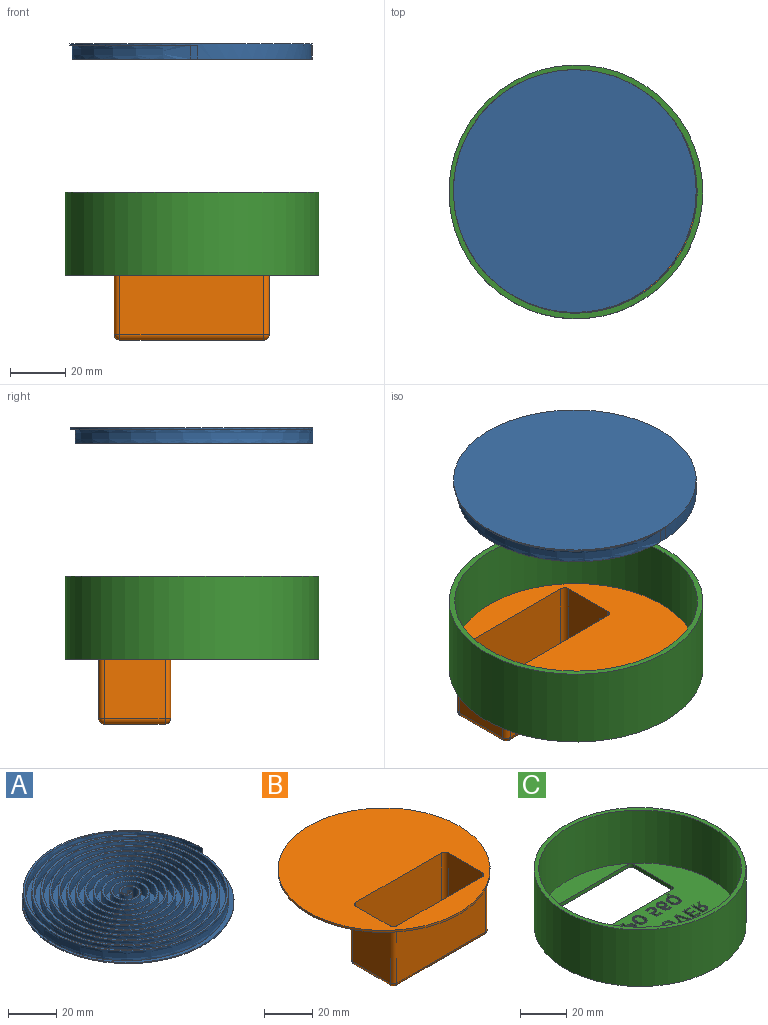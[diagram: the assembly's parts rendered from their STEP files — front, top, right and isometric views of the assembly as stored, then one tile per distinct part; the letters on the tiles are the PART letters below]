
ASSEMBLY  parts=3 mates=2
PART A: 9 faces, bbox 87.8x87.8x5.5 mm
  f0: plane 87.8x87.8mm, normal (0,0,1), area 4541mm2, adj f2,f3,f4,f5,f6,f7
  f1: plane 87.8x87.8mm, normal (0,0,-1), area 6054.5mm2, adj f2
  f2: cylinder r=43.9mm len=87.8mm, axis (0,0,1), area 450.2mm2, adj f0,f1,f3,f4,f8
  f3: cylinder r=43.87mm len=5mm, axis (0,0,-1), area 19.8mm2, adj f0,f2,f7,f8
  f4: cylinder r=43.3mm len=5mm, axis (0,0,-1), area 12.8mm2, adj f0,f2,f5,f8
  f5: extruded ~82.3x76.86mm, area 8343.7mm2, adj f0,f4,f6,f8
  f6: plane 5x0.36mm, normal (-0.71,-0.71,0), area 2.6mm2, adj f0,f5,f7,f8
  f7: extruded ~82.3x76.86mm, area 8343.7mm2, adj f0,f3,f6,f8
  f8: plane 86.84x85.93mm, normal (0,0,1), area 1513.4mm2, adj f2,f3,f4,f5,f6,f7
PART B: 38 faces, bbox 87.8x87.8x30 mm
  f0: plane 87.8x87.8mm, normal (0,0,1), area 4761.9mm2, adj f1,f12,f13,f14,f15,f16,f17,f18
  f1: cylinder r=43.9mm len=87.8mm, axis (0,0,1), area 275.8mm2, adj f0,f2
  f2: plane 87.8x87.8mm, normal (0,0,-1), area 4601.9mm2, adj f1,f3,f4,f5,f6,f7,f8,f9
  f3: plane 52x27mm, normal (0,1,0), area 1404mm2, adj f2,f4,f10,f33
  f4: cylinder r=2mm len=27mm, axis (0,0,1), area 84.8mm2, adj f2,f3,f5,f31
  f5: plane 27x22mm, normal (-1,0,0), area 586.9mm2, adj f2,f4,f6,f29,f37
  f6: cylinder r=2mm len=27mm, axis (0,0,1), area 84.8mm2, adj f2,f5,f7,f30
  f7: plane 52x27mm, normal (0,-1,0), area 1404mm2, adj f2,f6,f8,f32
  f8: cylinder r=2mm len=27mm, axis (0,0,1), area 84.8mm2, adj f2,f7,f9,f34
  f9: plane 27x22mm, normal (1,0,0), area 594mm2, adj f2,f8,f10,f36
  f10: cylinder r=2mm len=27mm, axis (0,0,1), area 84.8mm2, adj f2,f3,f9,f35
  f11: plane 52x22mm, normal (0,0,-1), area 1144mm2, adj f29,f32,f33,f36
  f12: plane 50x27mm, normal (0,-1,0), area 1350mm2, adj f0,f13,f19,f25
  f13: cylinder r=2mm len=27mm, axis (0,0,1), area 84.8mm2, adj f0,f12,f14,f23
  f14: plane 27x20mm, normal (1,0,0), area 532.9mm2, adj f0,f13,f15,f21,f37
  f15: cylinder r=2mm len=27mm, axis (0,0,1), area 84.8mm2, adj f0,f14,f16,f22
  f16: plane 50x27mm, normal (0,1,0), area 1350mm2, adj f0,f15,f17,f24
  f17: cylinder r=2mm len=27mm, axis (0,0,1), area 84.8mm2, adj f0,f16,f18,f26
  f18: plane 27x20mm, normal (-1,0,0), area 540mm2, adj f0,f17,f19,f28
  f19: cylinder r=2mm len=27mm, axis (0,0,1), area 84.8mm2, adj f0,f12,f18,f27
  f20: plane 50x20mm, normal (0,0,1), area 1000mm2, adj f21,f24,f25,f28
  f21: cylinder r=2mm len=20mm, axis (0,-1,0), area 62.8mm2, adj f14,f20,f22,f23
  f22: sphere r=2mm, area 6.3mm2, adj f15,f21,f24
  f23: sphere r=2mm, area 6.3mm2, adj f13,f21,f25
  f24: cylinder r=2mm len=50mm, axis (1,0,0), area 157.1mm2, adj f16,f20,f22,f26
  f25: cylinder r=2mm len=50mm, axis (-1,0,0), area 157.1mm2, adj f12,f20,f23,f27
  f26: sphere r=2mm, area 6.3mm2, adj f17,f24,f28
  f27: sphere r=2mm, area 6.3mm2, adj f19,f25,f28
  f28: cylinder r=2mm len=20mm, axis (0,1,0), area 62.8mm2, adj f18,f20,f26,f27
  f29: cylinder r=2mm len=22mm, axis (0,1,0), area 69.1mm2, adj f5,f11,f30,f31
  f30: sphere r=2mm, area 6.3mm2, adj f6,f29,f32
  f31: sphere r=2mm, area 6.3mm2, adj f4,f29,f33
  f32: cylinder r=2mm len=52mm, axis (-1,0,0), area 163.4mm2, adj f7,f11,f30,f34
  f33: cylinder r=2mm len=52mm, axis (1,0,0), area 163.4mm2, adj f3,f11,f31,f35
  f34: sphere r=2mm, area 6.3mm2, adj f8,f32,f36
  f35: sphere r=2mm, area 6.3mm2, adj f10,f33,f36
  f36: cylinder r=2mm len=22mm, axis (0,-1,0), area 69.1mm2, adj f9,f11,f34,f35
  f37: cylinder r=1.5mm len=3mm, axis (-1,0,0), area 9.4mm2, adj f5,f14
PART C: 428 faces, bbox 91.8x91.8x30 mm
  f0: plane 91.8x91.8mm, normal (0,0,-1), area 4849.9mm2, adj f4,f5,f6,f7,f8,f9,f10,f11
  f1: plane 87.8x87.8mm, normal (0,0,1), area 4285.7mm2, adj f2,f5,f6,f7,f8,f9,f10,f11
  f2: cylinder r=43.9mm len=87.8mm, axis (0,0,1), area 7723.3mm2, adj f1,f3
  f3: plane 91.8x91.8mm, normal (0,0,1), area 564.2mm2, adj f2,f4
  f4: cylinder r=45.9mm len=91.8mm, axis (0,0,1), area 8651.9mm2, adj f0,f3
  f5: cylinder r=2mm len=2mm, axis (0,0,-1), area 6.3mm2, adj f0,f1,f6,f12
  f6: plane 53x2mm, normal (0,1,0), area 106mm2, adj f0,f1,f5,f7
  f7: cylinder r=2mm len=2mm, axis (0,0,-1), area 6.3mm2, adj f0,f1,f6,f8
  f8: plane 23x2mm, normal (1,0,0), area 46mm2, adj f0,f1,f7,f9
  f9: cylinder r=2mm len=2mm, axis (0,0,-1), area 6.3mm2, adj f0,f1,f8,f10
  f10: plane 53x2mm, normal (0,-1,0), area 106mm2, adj f0,f1,f9,f11
  f11: cylinder r=2mm len=2mm, axis (0,0,-1), area 6.3mm2, adj f0,f1,f10,f12
  f12: plane 23x2mm, normal (-1,0,0), area 46mm2, adj f0,f1,f5,f11
  f13: plane 6.76x2mm, normal (1,0,0), area 13.5mm2, adj f0,f1,f14,f16
  f14: plane 2x1.12mm, normal (0,-1,0), area 2.2mm2, adj f0,f1,f13,f15
  f15: plane 6.76x2mm, normal (-1,0,0), area 13.5mm2, adj f0,f1,f14,f16
  f16: plane 2x1.12mm, normal (0,1,0), area 2.2mm2, adj f0,f1,f13,f15
  f17: extruded ~2x1.44mm, area 2.9mm2, adj f0,f1,f18,f37
  f18: extruded ~2x1.06mm, area 2.4mm2, adj f0,f1,f17,f19
  f19: extruded ~2x0.83mm, area 2.2mm2, adj f0,f1,f18,f20
  f20: extruded ~2x1.04mm, area 2.2mm2, adj f0,f1,f19,f21
  f21: plane 2x0.91mm, normal (1,0,0), area 1.8mm2, adj f0,f1,f20,f22
  f22: extruded ~2x0.57mm, area 1.2mm2, adj f0,f1,f21,f23
  f23: extruded ~2x0.48mm, area 1.3mm2, adj f0,f1,f22,f24
  f24: extruded ~2x0.77mm, area 1.7mm2, adj f0,f1,f23,f25
  f25: extruded ~2x1.11mm, area 2.2mm2, adj f0,f1,f24,f26
  f26: extruded ~2x1.11mm, area 2.2mm2, adj f0,f1,f25,f27
  f27: extruded ~2x0.77mm, area 1.7mm2, adj f0,f1,f26,f28
  f28: extruded ~2x0.47mm, area 1.3mm2, adj f0,f1,f27,f29
  f29: extruded ~2x0.58mm, area 1.2mm2, adj f0,f1,f28,f30
  f30: plane 2x1.36mm, normal (1,0,0), area 2.7mm2, adj f0,f1,f29,f31
  f31: plane 2x1.05mm, normal (0.86,-0.5,0), area 2.4mm2, adj f0,f1,f30,f32
  f32: plane 2x1.21mm, normal (0,-1,0), area 2.4mm2, adj f0,f1,f31,f33
  f33: plane 2x1.63mm, normal (-0.79,0.61,0), area 4.1mm2, adj f0,f1,f32,f34
  f34: extruded ~2x0.8mm, area 1.8mm2, adj f0,f1,f33,f35
  f35: extruded ~2x0.71mm, area 1.9mm2, adj f0,f1,f34,f36
  f36: extruded ~2x1mm, area 2.2mm2, adj f0,f1,f35,f37
  f37: extruded ~2x1.27mm, area 2.6mm2, adj f0,f1,f17,f36
  f38: extruded ~2x1.4mm, area 2.8mm2, adj f0,f1,f39,f56
  f39: extruded ~2x1.05mm, area 2.3mm2, adj f0,f1,f38,f40
  f40: extruded ~2x0.78mm, area 2.1mm2, adj f0,f1,f39,f41
  f41: extruded ~2x0.99mm, area 2.1mm2, adj f0,f1,f40,f42
  f42: plane 2x0.17mm, normal (0,-1,0), area 0.3mm2, adj f0,f1,f41,f43
  f43: plane 2x0.89mm, normal (-1,0,0), area 1.8mm2, adj f0,f1,f42,f44
  f44: extruded ~2x0.57mm, area 1.2mm2, adj f0,f1,f43,f45
  f45: extruded ~2x0.48mm, area 1.4mm2, adj f0,f1,f44,f46
  f46: extruded ~2x0.77mm, area 1.7mm2, adj f0,f1,f45,f47
  f47: extruded ~2x1.11mm, area 2.2mm2, adj f0,f1,f46,f48
  f48: extruded ~2x1.11mm, area 2.2mm2, adj f0,f1,f47,f49
  f49: extruded ~2x0.77mm, area 1.7mm2, adj f0,f1,f48,f50
  f50: extruded ~2x0.47mm, area 1.3mm2, adj f0,f1,f49,f51
  f51: extruded ~2x0.58mm, area 1.2mm2, adj f0,f1,f50,f52
  f52: plane 2x0.92mm, normal (-1,0,0), area 1.8mm2, adj f0,f1,f51,f53
  f53: extruded ~2x1.05mm, area 2.2mm2, adj f0,f1,f52,f54
  f54: extruded ~2x0.84mm, area 2.2mm2, adj f0,f1,f53,f55
  f55: extruded ~2x1.06mm, area 2.4mm2, adj f0,f1,f54,f56
  f56: extruded ~2x1.44mm, area 2.9mm2, adj f0,f1,f38,f55
  f57: extruded ~2x0.72mm, area 1.5mm2, adj f0,f1,f58,f87
  f58: extruded ~2x0.57mm, area 1.2mm2, adj f0,f1,f57,f59
  f59: plane 2x0.76mm, normal (-0.91,-0.42,0), area 1.7mm2, adj f0,f1,f58,f60
  f60: extruded ~2x0.78mm, area 1.7mm2, adj f0,f1,f59,f61
  f61: extruded ~2x0.97mm, area 1.9mm2, adj f0,f1,f60,f62
  f62: extruded ~2x0.87mm, area 1.8mm2, adj f0,f1,f61,f63
  f63: extruded ~2x0.79mm, area 2.1mm2, adj f0,f1,f62,f64
  f64: extruded ~2x1.27mm, area 2.8mm2, adj f0,f1,f63,f65
  f65: extruded ~2.01x2mm, area 4.1mm2, adj f0,f1,f64,f66
  f66: extruded ~2x1.06mm, area 2.1mm2, adj f0,f1,f65,f67
  f67: extruded ~2x0.85mm, area 1.9mm2, adj f0,f1,f66,f68
  f68: extruded ~2x0.7mm, area 1.8mm2, adj f0,f1,f67,f69
  f69: extruded ~2x0.98mm, area 2mm2, adj f0,f1,f68,f70
  f70: plane 2x0.9mm, normal (-1,0,0), area 1.8mm2, adj f0,f1,f69,f71
  f71: extruded ~2x0.46mm, area 1mm2, adj f0,f1,f70,f72
  f72: extruded ~2x0.37mm, area 1mm2, adj f0,f1,f71,f73
  f73: extruded ~2x0.45mm, area 1mm2, adj f0,f1,f72,f74
  f74: extruded ~2x0.56mm, area 1.1mm2, adj f0,f1,f73,f75
  f75: extruded ~2x0.55mm, area 1.1mm2, adj f0,f1,f74,f76
  f76: extruded ~2x0.44mm, area 1mm2, adj f0,f1,f75,f77
  f77: extruded ~2x0.37mm, area 1mm2, adj f0,f1,f76,f78
  f78: extruded ~2x0.47mm, area 1mm2, adj f0,f1,f77,f79
  f79: plane 2x0.81mm, normal (-1,0,0), area 1.6mm2, adj f0,f1,f78,f80
  f80: extruded ~2x0.67mm, area 1.4mm2, adj f0,f1,f79,f81
  f81: extruded ~2x0.39mm, area 1.1mm2, adj f0,f1,f80,f82
  f82: extruded ~2x0.04mm, area 0.1mm2, adj f0,f1,f81,f83
  f83: extruded ~2x0.04mm, area 0.1mm2, adj f0,f1,f82,f84
  f84: extruded ~2x0.74mm, area 1.5mm2, adj f0,f1,f83,f85
  f85: extruded ~2x0.63mm, area 1.4mm2, adj f0,f1,f84,f86
  f86: extruded ~2x0.45mm, area 1.3mm2, adj f0,f1,f85,f87
  f87: extruded ~2x0.65mm, area 1.4mm2, adj f0,f1,f57,f86
  f88: plane 2x0.83mm, normal (1,0,0), area 1.7mm2, adj f0,f1,f89,f101
  f89: extruded ~2x0.76mm, area 1.8mm2, adj f0,f1,f88,f90
  f90: extruded ~2x0.95mm, area 2mm2, adj f0,f1,f89,f91
  f91: extruded ~2x0.98mm, area 2.1mm2, adj f0,f1,f90,f92
  f92: extruded ~2x0.76mm, area 1.8mm2, adj f0,f1,f91,f93
  f93: plane 2x0.9mm, normal (1,0,0), area 1.8mm2, adj f0,f1,f92,f94
  f94: extruded ~2x0.68mm, area 1.4mm2, adj f0,f1,f93,f95
  f95: extruded ~2x0.66mm, area 1.6mm2, adj f0,f1,f94,f96
  f96: extruded ~2x0.74mm, area 1.8mm2, adj f0,f1,f95,f97
  f97: extruded ~2x1.11mm, area 2.3mm2, adj f0,f1,f96,f98
  f98: extruded ~2x0.76mm, area 1.5mm2, adj f0,f1,f97,f99
  f99: extruded ~2x0.69mm, area 1.6mm2, adj f0,f1,f98,f100
  f100: extruded ~2x0.64mm, area 1.6mm2, adj f0,f1,f99,f101
  f101: extruded ~2x0.83mm, area 1.7mm2, adj f0,f1,f88,f100
  f102: plane 2x0.83mm, normal (1,0,0), area 1.7mm2, adj f0,f1,f103,f105
  f103: plane 2.73x2mm, normal (0,-1,0), area 5.5mm2, adj f0,f1,f102,f104
  f104: plane 2x0.83mm, normal (-1,0,0), area 1.7mm2, adj f0,f1,f103,f105
  f105: plane 2.73x2mm, normal (0,1,0), area 5.5mm2, adj f0,f1,f102,f104
  f106: plane 2x0.75mm, normal (-1,0,0), area 1.5mm2, adj f0,f1,f107,f109
  f107: plane 2.45x2mm, normal (0,1,0), area 4.9mm2, adj f0,f1,f106,f108
  f108: plane 2x0.75mm, normal (1,0,0), area 1.5mm2, adj f0,f1,f107,f109
  f109: plane 2.45x2mm, normal (0,-1,0), area 4.9mm2, adj f0,f1,f106,f108
  f110: plane 6.76x2mm, normal (1,0,0), area 13.5mm2, adj f0,f1,f111,f113
  f111: plane 2x1.12mm, normal (0,-1,0), area 2.2mm2, adj f0,f1,f110,f112
  f112: plane 6.76x2mm, normal (-1,0,0), area 13.5mm2, adj f0,f1,f111,f113
  f113: plane 2x1.12mm, normal (0,1,0), area 2.2mm2, adj f0,f1,f110,f112
  f114: plane 5x2mm, normal (0.96,0.27,0), area 10.4mm2, adj f0,f1,f115,f118
  f115: plane 2x1.79mm, normal (1,0,0), area 3.6mm2, adj f0,f1,f114,f116
  f116: plane 2x0.48mm, normal (0,-1,0), area 1mm2, adj f0,f1,f115,f117
  f117: plane 6.79x2.2mm, normal (-0.95,-0.31,0), area 14.3mm2, adj f0,f1,f116,f118
  f118: plane 2x1.25mm, normal (0,1,0), area 2.5mm2, adj f0,f1,f114,f117
  f119: plane 6.79x2.1mm, normal (0.96,-0.3,0), area 14.2mm2, adj f0,f1,f120,f123
  f120: plane 2x0.58mm, normal (0,-1,0), area 1.2mm2, adj f0,f1,f119,f121
  f121: plane 2x1.49mm, normal (-1,0,0), area 3mm2, adj f0,f1,f120,f122
  f122: plane 5.3x2mm, normal (-0.97,0.26,0), area 11mm2, adj f0,f1,f121,f123
  f123: plane 2x1.26mm, normal (0,1,0), area 2.5mm2, adj f0,f1,f119,f122
  f124: plane 2x0.91mm, normal (1,0,0), area 1.8mm2, adj f0,f1,f125,f141
  f125: extruded ~2x0.58mm, area 1.2mm2, adj f0,f1,f124,f126
  f126: extruded ~2x0.48mm, area 1.4mm2, adj f0,f1,f125,f127
  f127: extruded ~2x0.77mm, area 1.7mm2, adj f0,f1,f126,f128
  f128: extruded ~2x1.11mm, area 2.2mm2, adj f0,f1,f127,f129
  f129: extruded ~2x1.11mm, area 2.2mm2, adj f0,f1,f128,f130
  f130: extruded ~2x0.77mm, area 1.7mm2, adj f0,f1,f129,f131
  f131: extruded ~2x0.48mm, area 1.3mm2, adj f0,f1,f130,f132
  f132: extruded ~2x0.59mm, area 1.2mm2, adj f0,f1,f131,f133
  f133: plane 2x0.91mm, normal (1,0,0), area 1.8mm2, adj f0,f1,f132,f134
  f134: extruded ~2x1.05mm, area 2.2mm2, adj f0,f1,f133,f135
  f135: extruded ~2x0.83mm, area 2.1mm2, adj f0,f1,f134,f136
  f136: extruded ~2x1.07mm, area 2.4mm2, adj f0,f1,f135,f137
  f137: extruded ~2x1.45mm, area 2.9mm2, adj f0,f1,f136,f138
  f138: extruded ~2x1.44mm, area 2.9mm2, adj f0,f1,f137,f139
  f139: extruded ~2x1.06mm, area 2.4mm2, adj f0,f1,f138,f140
  f140: extruded ~2x0.83mm, area 2.2mm2, adj f0,f1,f139,f141
  f141: extruded ~2x1.04mm, area 2.2mm2, adj f0,f1,f124,f140
  f142: extruded ~2x1.45mm, area 2.9mm2, adj f0,f1,f143,f159
  f143: extruded ~2x1.07mm, area 2.4mm2, adj f0,f1,f142,f144
  f144: extruded ~2x0.84mm, area 2.2mm2, adj f0,f1,f143,f145
  f145: extruded ~2x1.05mm, area 2.2mm2, adj f0,f1,f144,f146
  f146: plane 2x0.91mm, normal (-1,0,0), area 1.8mm2, adj f0,f1,f145,f147
  f147: extruded ~2x0.58mm, area 1.2mm2, adj f0,f1,f146,f148
  f148: extruded ~2x0.48mm, area 1.4mm2, adj f0,f1,f147,f149
  f149: extruded ~2x0.77mm, area 1.7mm2, adj f0,f1,f148,f150
  f150: extruded ~2x1.11mm, area 2.2mm2, adj f0,f1,f149,f151
  f151: extruded ~2x1.11mm, area 2.2mm2, adj f0,f1,f150,f152
  f152: extruded ~2x0.77mm, area 1.7mm2, adj f0,f1,f151,f153
  f153: extruded ~2x0.48mm, area 1.3mm2, adj f0,f1,f152,f154
  f154: extruded ~2x0.59mm, area 1.2mm2, adj f0,f1,f153,f155
  f155: plane 2x0.92mm, normal (-1,0,0), area 1.8mm2, adj f0,f1,f154,f156
  f156: extruded ~2x1.05mm, area 2.2mm2, adj f0,f1,f155,f157
  f157: extruded ~2x0.83mm, area 2.2mm2, adj f0,f1,f156,f158
  f158: extruded ~2x1.06mm, area 2.4mm2, adj f0,f1,f157,f159
  f159: extruded ~2x1.44mm, area 2.9mm2, adj f0,f1,f142,f158
  f160: extruded ~2x1.44mm, area 2.9mm2, adj f0,f1,f161,f177
  f161: extruded ~2x1.06mm, area 2.4mm2, adj f0,f1,f160,f162
  f162: extruded ~2x0.82mm, area 2.1mm2, adj f0,f1,f161,f163
  f163: extruded ~2x1.03mm, area 2.2mm2, adj f0,f1,f162,f164
  f164: plane 2x0.9mm, normal (-1,0,0), area 1.8mm2, adj f0,f1,f163,f165
  f165: extruded ~2x0.56mm, area 1.2mm2, adj f0,f1,f164,f166
  f166: extruded ~2x0.48mm, area 1.4mm2, adj f0,f1,f165,f167
  f167: extruded ~2x0.77mm, area 1.7mm2, adj f0,f1,f166,f168
  f168: extruded ~2x1.1mm, area 2.2mm2, adj f0,f1,f167,f169
  f169: extruded ~2x1.1mm, area 2.2mm2, adj f0,f1,f168,f170
  f170: extruded ~2x0.77mm, area 1.7mm2, adj f0,f1,f169,f171
  f171: extruded ~2x0.47mm, area 1.3mm2, adj f0,f1,f170,f172
  f172: extruded ~2x0.57mm, area 1.2mm2, adj f0,f1,f171,f173
  f173: plane 2x0.92mm, normal (-1,0,0), area 1.8mm2, adj f0,f1,f172,f174
  f174: extruded ~2x1.03mm, area 2.2mm2, adj f0,f1,f173,f175
  f175: extruded ~2x0.82mm, area 2.1mm2, adj f0,f1,f174,f176
  f176: extruded ~2x1.05mm, area 2.4mm2, adj f0,f1,f175,f177
  f177: extruded ~2x1.44mm, area 2.9mm2, adj f0,f1,f160,f176
  f178: plane 2x0.75mm, normal (-1,0,0), area 1.5mm2, adj f0,f1,f179,f181
  f179: plane 2.45x2mm, normal (0,1,0), area 4.9mm2, adj f0,f1,f178,f180
  f180: plane 2x0.75mm, normal (1,0,0), area 1.5mm2, adj f0,f1,f179,f181
  f181: plane 2.45x2mm, normal (0,-1,0), area 4.9mm2, adj f0,f1,f178,f180
  f182: plane 2.73x2mm, normal (0,1,0), area 5.5mm2, adj f0,f1,f183,f185
  f183: plane 2x0.83mm, normal (1,0,0), area 1.7mm2, adj f0,f1,f182,f184
  f184: plane 2.73x2mm, normal (0,-1,0), area 5.5mm2, adj f0,f1,f183,f185
  f185: plane 2x0.83mm, normal (-1,0,0), area 1.7mm2, adj f0,f1,f182,f184
  f186: plane 2x1.12mm, normal (0,1,0), area 2.2mm2, adj f0,f1,f187,f191
  f187: plane 6.76x2mm, normal (1,0,0), area 13.5mm2, adj f0,f1,f186,f188
  f188: plane 4.23x2mm, normal (0,-1,0), area 8.5mm2, adj f0,f1,f187,f189
  f189: plane 2x0.83mm, normal (-1,0,0), area 1.7mm2, adj f0,f1,f188,f190
  f190: plane 3.11x2mm, normal (0,1,0), area 6.2mm2, adj f0,f1,f189,f191
  f191: plane 5.92x2mm, normal (-1,0,0), area 11.8mm2, adj f0,f1,f186,f190
  f192: plane 6.75x2.35mm, normal (-0.94,0.33,0), area 14.3mm2, adj f0,f1,f193,f198
  f193: plane 2x1.09mm, normal (0,1,0), area 2.2mm2, adj f0,f1,f192,f194
  f194: plane 6.75x2.36mm, normal (0.94,0.33,0), area 14.3mm2, adj f0,f1,f193,f195
  f195: plane 2x1.15mm, normal (0,-1,0), area 2.3mm2, adj f0,f1,f194,f196
  f196: plane 5.06x2mm, normal (-0.94,-0.33,0), area 10.7mm2, adj f0,f1,f195,f197
  f197: plane 5.06x2mm, normal (0.95,-0.33,0), area 10.7mm2, adj f0,f1,f196,f198
  f198: plane 2x1.14mm, normal (0,-1,0), area 2.3mm2, adj f0,f1,f192,f197
  f199: plane 2x1.23mm, normal (0,1,0), area 2.5mm2, adj f0,f1,f200,f202
  f200: plane 2x0.74mm, normal (0.95,0.33,0), area 1.6mm2, adj f0,f1,f199,f201
  f201: plane 2x1.75mm, normal (0,-1,0), area 3.5mm2, adj f0,f1,f200,f202
  f202: plane 2x0.74mm, normal (-0.94,0.34,0), area 1.6mm2, adj f0,f1,f199,f201
  f203: plane 5.14x2mm, normal (0,1,0), area 10.3mm2, adj f0,f1,f204,f210
  f204: plane 2x0.75mm, normal (1,0,0), area 1.5mm2, adj f0,f1,f203,f205
  f205: plane 2.02x2mm, normal (0,-1,0), area 4mm2, adj f0,f1,f204,f206
  f206: plane 6.01x2mm, normal (1,0,0), area 12mm2, adj f0,f1,f205,f207
  f207: plane 2x1.11mm, normal (0,-1,0), area 2.2mm2, adj f0,f1,f206,f208
  f208: plane 6.01x2mm, normal (-1,0,0), area 12mm2, adj f0,f1,f207,f209
  f209: plane 2.02x2mm, normal (0,-1,0), area 4mm2, adj f0,f1,f208,f210
  f210: plane 2x0.75mm, normal (-1,0,0), area 1.5mm2, adj f0,f1,f203,f209
  f211: plane 2x0.76mm, normal (-0.66,-0.75,0), area 2mm2, adj f0,f1,f212,f215
  f212: extruded ~2x1.72mm, area 3.8mm2, adj f0,f1,f211,f213
  f213: plane 2x0.91mm, normal (1,0,0), area 1.8mm2, adj f0,f1,f212,f214
  f214: extruded ~2x0.51mm, area 1.1mm2, adj f0,f1,f213,f215
  f215: extruded ~2x0.45mm, area 1.2mm2, adj f0,f1,f211,f214
  f216: plane 2x0.91mm, normal (1,0,0), area 1.8mm2, adj f0,f1,f217,f221
  f217: extruded ~2x0.94mm, area 1.9mm2, adj f0,f1,f216,f218
  f218: extruded ~2x0.78mm, area 1.9mm2, adj f0,f1,f217,f219
  f219: plane 2x0.76mm, normal (-0.66,0.75,0), area 2mm2, adj f0,f1,f218,f220
  f220: extruded ~2x0.44mm, area 1.1mm2, adj f0,f1,f219,f221
  f221: extruded ~2x0.52mm, area 1.1mm2, adj f0,f1,f216,f220
  f222: extruded ~2x0.32mm, area 0.6mm2, adj f0,f1,f223,f247
  f223: extruded ~2x0.39mm, area 0.8mm2, adj f0,f1,f222,f224
  f224: plane 2x0.91mm, normal (0.99,0.12,0), area 1.8mm2, adj f0,f1,f223,f225
  f225: extruded ~2x0.33mm, area 0.7mm2, adj f0,f1,f224,f226
  f226: extruded ~2x0.35mm, area 0.7mm2, adj f0,f1,f225,f227
  f227: extruded ~2x0.88mm, area 1.9mm2, adj f0,f1,f226,f228
  f228: extruded ~2x0.83mm, area 1.8mm2, adj f0,f1,f227,f229
  f229: extruded ~2x1.07mm, area 2.3mm2, adj f0,f1,f228,f230
  f230: extruded ~2x1.06mm, area 2.3mm2, adj f0,f1,f229,f231
  f231: extruded ~2x0.45mm, area 0.9mm2, adj f0,f1,f230,f232
  f232: extruded ~2x0.46mm, area 1mm2, adj f0,f1,f231,f233
  f233: extruded ~2x0.42mm, area 0.9mm2, adj f0,f1,f232,f234
  f234: extruded ~2x0.33mm, area 0.7mm2, adj f0,f1,f233,f235
  f235: plane 2x0.92mm, normal (1,0,0), area 1.8mm2, adj f0,f1,f234,f236
  f236: extruded ~2x0.27mm, area 0.6mm2, adj f0,f1,f235,f237
  f237: extruded ~2x0.41mm, area 0.9mm2, adj f0,f1,f236,f238
  f238: extruded ~2x0.52mm, area 1.1mm2, adj f0,f1,f237,f239
  f239: extruded ~2x0.6mm, area 1.2mm2, adj f0,f1,f238,f240
  f240: extruded ~2x0.68mm, area 1.4mm2, adj f0,f1,f239,f241
  f241: extruded ~2x0.76mm, area 1.6mm2, adj f0,f1,f240,f242
  f242: extruded ~2x0.68mm, area 1.8mm2, adj f0,f1,f241,f243
  f243: extruded ~2x1.2mm, area 2.5mm2, adj f0,f1,f242,f244
  f244: extruded ~2x0.74mm, area 1.5mm2, adj f0,f1,f243,f245
  f245: extruded ~2x0.64mm, area 1.5mm2, adj f0,f1,f244,f246
  f246: extruded ~2x0.65mm, area 1.6mm2, adj f0,f1,f245,f247
  f247: extruded ~2x0.86mm, area 1.8mm2, adj f0,f1,f222,f246
  f248: plane 2x0.37mm, normal (-0.99,-0.12,0), area 0.7mm2, adj f0,f1,f249,f262
  f249: plane 2x0.61mm, normal (-0.99,-0.12,0), area 1.2mm2, adj f0,f1,f248,f250
  f250: extruded ~2x0.05mm, area 0.1mm2, adj f0,f1,f249,f251
  f251: extruded ~2x0.22mm, area 0.5mm2, adj f0,f1,f250,f252
  f252: extruded ~2x0.56mm, area 1.1mm2, adj f0,f1,f251,f253
  f253: extruded ~2x1.05mm, area 2.1mm2, adj f0,f1,f252,f254
  f254: plane 2.52x2mm, normal (0,-1,0), area 5mm2, adj f0,f1,f253,f255
  f255: plane 2x0.9mm, normal (-1,0,0), area 1.8mm2, adj f0,f1,f254,f256
  f256: plane 3.35x2mm, normal (0,1,0), area 6.7mm2, adj f0,f1,f255,f257
  f257: extruded ~2x1.73mm, area 3.5mm2, adj f0,f1,f256,f258
  f258: extruded ~2x0.67mm, area 1.3mm2, adj f0,f1,f257,f259
  f259: extruded ~2x0.61mm, area 1.2mm2, adj f0,f1,f258,f260
  f260: extruded ~2x0.48mm, area 1mm2, adj f0,f1,f259,f261
  f261: extruded ~2x0.28mm, area 0.6mm2, adj f0,f1,f260,f262
  f262: plane 2x0.86mm, normal (0,-1,0), area 1.7mm2, adj f0,f1,f248,f261
  f263: plane 2x0.91mm, normal (1,0,0), area 1.8mm2, adj f0,f1,f264,f280
  f264: extruded ~2x0.58mm, area 1.2mm2, adj f0,f1,f263,f265
  f265: extruded ~2x0.48mm, area 1.4mm2, adj f0,f1,f264,f266
  f266: extruded ~2x0.77mm, area 1.7mm2, adj f0,f1,f265,f267
  f267: extruded ~2x1.11mm, area 2.2mm2, adj f0,f1,f266,f268
  f268: extruded ~2x1.11mm, area 2.2mm2, adj f0,f1,f267,f269
  f269: extruded ~2x0.77mm, area 1.7mm2, adj f0,f1,f268,f270
  f270: extruded ~2x0.48mm, area 1.3mm2, adj f0,f1,f269,f271
  f271: extruded ~2x0.59mm, area 1.2mm2, adj f0,f1,f270,f272
  f272: plane 2x0.91mm, normal (1,0,0), area 1.8mm2, adj f0,f1,f271,f273
  f273: extruded ~2x1.05mm, area 2.2mm2, adj f0,f1,f272,f274
  f274: extruded ~2x0.83mm, area 2.1mm2, adj f0,f1,f273,f275
  f275: extruded ~2x1.07mm, area 2.4mm2, adj f0,f1,f274,f276
  f276: extruded ~2x1.45mm, area 2.9mm2, adj f0,f1,f275,f277
  f277: extruded ~2x1.44mm, area 2.9mm2, adj f0,f1,f276,f278
  f278: extruded ~2x1.06mm, area 2.4mm2, adj f0,f1,f277,f279
  f279: extruded ~2x0.83mm, area 2.2mm2, adj f0,f1,f278,f280
  f280: extruded ~2x1.04mm, area 2.2mm2, adj f0,f1,f263,f279
  f281: extruded ~2x1.45mm, area 2.9mm2, adj f0,f1,f282,f298
  f282: extruded ~2x1.07mm, area 2.4mm2, adj f0,f1,f281,f283
  f283: extruded ~2x0.84mm, area 2.2mm2, adj f0,f1,f282,f284
  f284: extruded ~2x1.05mm, area 2.2mm2, adj f0,f1,f283,f285
  f285: plane 2x0.91mm, normal (-1,0,0), area 1.8mm2, adj f0,f1,f284,f286
  f286: extruded ~2x0.58mm, area 1.2mm2, adj f0,f1,f285,f287
  f287: extruded ~2x0.48mm, area 1.4mm2, adj f0,f1,f286,f288
  f288: extruded ~2x0.77mm, area 1.7mm2, adj f0,f1,f287,f289
  f289: extruded ~2x1.11mm, area 2.2mm2, adj f0,f1,f288,f290
  f290: extruded ~2x1.11mm, area 2.2mm2, adj f0,f1,f289,f291
  f291: extruded ~2x0.77mm, area 1.7mm2, adj f0,f1,f290,f292
  f292: extruded ~2x0.48mm, area 1.3mm2, adj f0,f1,f291,f293
  f293: extruded ~2x0.59mm, area 1.2mm2, adj f0,f1,f292,f294
  f294: plane 2x0.92mm, normal (-1,0,0), area 1.8mm2, adj f0,f1,f293,f295
  f295: extruded ~2x1.05mm, area 2.2mm2, adj f0,f1,f294,f296
  f296: extruded ~2x0.83mm, area 2.2mm2, adj f0,f1,f295,f297
  f297: extruded ~2x1.06mm, area 2.4mm2, adj f0,f1,f296,f298
  f298: extruded ~2x1.44mm, area 2.9mm2, adj f0,f1,f281,f297
  f299: plane 2x0.47mm, normal (0,1,0), area 0.9mm2, adj f0,f1,f300,f320
  f300: plane 2x0.83mm, normal (1,0,0), area 1.7mm2, adj f0,f1,f299,f301
  f301: plane 2x0.45mm, normal (0,-1,0), area 0.9mm2, adj f0,f1,f300,f302
  f302: extruded ~2x0.68mm, area 1.4mm2, adj f0,f1,f301,f303
  f303: extruded ~2x0.4mm, area 1mm2, adj f0,f1,f302,f304
  f304: extruded ~2x0.41mm, area 0.9mm2, adj f0,f1,f303,f305
  f305: extruded ~2x0.38mm, area 0.8mm2, adj f0,f1,f304,f306
  f306: extruded ~2x0.69mm, area 1.4mm2, adj f0,f1,f305,f307
  f307: extruded ~2x0.44mm, area 1mm2, adj f0,f1,f306,f308
  f308: extruded ~2x0.36mm, area 0.9mm2, adj f0,f1,f307,f309
  f309: extruded ~2x0.4mm, area 0.8mm2, adj f0,f1,f308,f310
  f310: plane 2x0.63mm, normal (0,1,0), area 1.3mm2, adj f0,f1,f309,f311
  f311: plane 2x0.81mm, normal (1,0,0), area 1.6mm2, adj f0,f1,f310,f312
  f312: plane 2x0.44mm, normal (0,-1,0), area 0.9mm2, adj f0,f1,f311,f313
  f313: extruded ~2x0.97mm, area 2mm2, adj f0,f1,f312,f314
  f314: extruded ~2x0.75mm, area 1.8mm2, adj f0,f1,f313,f315
  f315: extruded ~2x0.7mm, area 1.7mm2, adj f0,f1,f314,f316
  f316: extruded ~2x0.93mm, area 1.9mm2, adj f0,f1,f315,f317
  f317: extruded ~2x0.88mm, area 1.8mm2, adj f0,f1,f316,f318
  f318: extruded ~2x0.66mm, area 1.7mm2, adj f0,f1,f317,f319
  f319: extruded ~2x0.76mm, area 1.7mm2, adj f0,f1,f318,f320
  f320: extruded ~2x0.85mm, area 1.7mm2, adj f0,f1,f299,f319
  f321: plane 6.76x2mm, normal (1,0,0), area 13.5mm2, adj f0,f1,f322,f324
  f322: plane 2x1.1mm, normal (0,-1,0), area 2.2mm2, adj f0,f1,f321,f323
  f323: plane 6.76x2mm, normal (-1,0,0), area 13.5mm2, adj f0,f1,f322,f324
  f324: plane 2x1.1mm, normal (0,1,0), area 2.2mm2, adj f0,f1,f321,f323
  f325: plane 6.75x2.35mm, normal (-0.94,0.33,0), area 14.3mm2, adj f0,f1,f326,f331
  f326: plane 2x1.09mm, normal (0,1,0), area 2.2mm2, adj f0,f1,f325,f327
  f327: plane 6.75x2.36mm, normal (0.94,0.33,0), area 14.3mm2, adj f0,f1,f326,f328
  f328: plane 2x1.15mm, normal (0,-1,0), area 2.3mm2, adj f0,f1,f327,f329
  f329: plane 5.06x2mm, normal (-0.94,-0.33,0), area 10.7mm2, adj f0,f1,f328,f330
  f330: plane 5.06x2mm, normal (0.95,-0.33,0), area 10.7mm2, adj f0,f1,f329,f331
  f331: plane 2x1.14mm, normal (0,-1,0), area 2.3mm2, adj f0,f1,f325,f330
  f332: plane 2x1.23mm, normal (0,1,0), area 2.5mm2, adj f0,f1,f333,f335
  f333: plane 2x0.74mm, normal (0.95,0.33,0), area 1.6mm2, adj f0,f1,f332,f334
  f334: plane 2x1.75mm, normal (0,-1,0), area 3.5mm2, adj f0,f1,f333,f335
  f335: plane 2x0.74mm, normal (-0.94,0.34,0), area 1.6mm2, adj f0,f1,f332,f334
  f336: plane 5.14x2mm, normal (0,1,0), area 10.3mm2, adj f0,f1,f337,f343
  f337: plane 2x0.75mm, normal (1,0,0), area 1.5mm2, adj f0,f1,f336,f338
  f338: plane 2.02x2mm, normal (0,-1,0), area 4mm2, adj f0,f1,f337,f339
  f339: plane 6.01x2mm, normal (1,0,0), area 12mm2, adj f0,f1,f338,f340
  f340: plane 2x1.11mm, normal (0,-1,0), area 2.2mm2, adj f0,f1,f339,f341
  f341: plane 6.01x2mm, normal (-1,0,0), area 12mm2, adj f0,f1,f340,f342
  f342: plane 2.02x2mm, normal (0,-1,0), area 4mm2, adj f0,f1,f341,f343
  f343: plane 2x0.75mm, normal (-1,0,0), area 1.5mm2, adj f0,f1,f336,f342
  f344: plane 2.66x2mm, normal (-0.87,0.5,0), area 6.1mm2, adj f0,f1,f345,f369
  f345: extruded ~2x0.92mm, area 2.4mm2, adj f0,f1,f344,f346
  f346: extruded ~2x1.25mm, area 2.6mm2, adj f0,f1,f345,f347
  f347: extruded ~2x0.88mm, area 1.8mm2, adj f0,f1,f346,f348
  f348: extruded ~2x0.66mm, area 1.7mm2, adj f0,f1,f347,f349
  f349: extruded ~2x0.76mm, area 1.7mm2, adj f0,f1,f348,f350
  f350: extruded ~2x0.85mm, area 1.7mm2, adj f0,f1,f349,f351
  f351: plane 2x0.47mm, normal (0,1,0), area 0.9mm2, adj f0,f1,f350,f352
  f352: plane 2x0.83mm, normal (1,0,0), area 1.7mm2, adj f0,f1,f351,f353
  f353: plane 2x0.45mm, normal (0,-1,0), area 0.9mm2, adj f0,f1,f352,f354
  f354: extruded ~2x0.68mm, area 1.4mm2, adj f0,f1,f353,f355
  f355: extruded ~2x0.4mm, area 1mm2, adj f0,f1,f354,f356
  f356: extruded ~2x0.41mm, area 0.9mm2, adj f0,f1,f355,f357
  f357: extruded ~2x0.38mm, area 0.8mm2, adj f0,f1,f356,f358
  f358: extruded ~2x0.69mm, area 1.4mm2, adj f0,f1,f357,f359
  f359: extruded ~2x0.44mm, area 1mm2, adj f0,f1,f358,f360
  f360: extruded ~2x0.37mm, area 0.9mm2, adj f0,f1,f359,f361
  f361: extruded ~2x0.4mm, area 0.8mm2, adj f0,f1,f360,f362
  f362: plane 2x0.62mm, normal (0,1,0), area 1.2mm2, adj f0,f1,f361,f363
  f363: plane 2x0.81mm, normal (1,0,0), area 1.6mm2, adj f0,f1,f362,f364
  f364: plane 2x0.33mm, normal (0,-1,0), area 0.6mm2, adj f0,f1,f363,f365
  f365: plane 2x0.19mm, normal (0,-1,0), area 0.4mm2, adj f0,f1,f364,f366
  f366: extruded ~2x0.1mm, area 0.2mm2, adj f0,f1,f365,f367
  f367: extruded ~2x0.06mm, area 0.1mm2, adj f0,f1,f366,f368
  f368: plane 2.45x2mm, normal (0.89,-0.46,0), area 5.5mm2, adj f0,f1,f367,f369
  f369: plane 2x1.16mm, normal (0,-1,0), area 2.3mm2, adj f0,f1,f344,f368
  f370: plane 6.76x2mm, normal (1,0,0), area 13.5mm2, adj f0,f1,f371,f373
  f371: plane 2x1.1mm, normal (0,-1,0), area 2.2mm2, adj f0,f1,f370,f372
  f372: plane 6.76x2mm, normal (-1,0,0), area 13.5mm2, adj f0,f1,f371,f373
  f373: plane 2x1.1mm, normal (0,1,0), area 2.2mm2, adj f0,f1,f370,f372
  f374: plane 2.73x2mm, normal (0,1,0), area 5.5mm2, adj f0,f1,f375,f377
  f375: plane 2x0.83mm, normal (1,0,0), area 1.7mm2, adj f0,f1,f374,f376
  f376: plane 2.73x2mm, normal (0,-1,0), area 5.5mm2, adj f0,f1,f375,f377
  f377: plane 2x0.83mm, normal (-1,0,0), area 1.7mm2, adj f0,f1,f374,f376
  f378: plane 2x1.07mm, normal (1,0,0), area 2.1mm2, adj f0,f1,f379,f390
  f379: extruded ~2x0.54mm, area 1.3mm2, adj f0,f1,f378,f380
  f380: extruded ~2x0.53mm, area 1.2mm2, adj f0,f1,f379,f381
  f381: extruded ~2x1mm, area 2.7mm2, adj f0,f1,f380,f382
  f382: plane 2x0.88mm, normal (1,0,0), area 1.8mm2, adj f0,f1,f381,f383
  f383: extruded ~2x0.75mm, area 1.6mm2, adj f0,f1,f382,f384
  f384: extruded ~2x0.56mm, area 1.4mm2, adj f0,f1,f383,f385
  f385: extruded ~2x0.56mm, area 1.3mm2, adj f0,f1,f384,f386
  f386: extruded ~2x0.64mm, area 1.3mm2, adj f0,f1,f385,f387
  f387: extruded ~2x0.8mm, area 1.6mm2, adj f0,f1,f386,f388
  f388: extruded ~2x0.55mm, area 1.4mm2, adj f0,f1,f387,f389
  f389: extruded ~2x0.57mm, area 1.4mm2, adj f0,f1,f388,f390
  f390: extruded ~2x0.62mm, area 1.4mm2, adj f0,f1,f378,f389
  f391: plane 2x0.79mm, normal (0.97,0.24,0), area 1.6mm2, adj f0,f1,f392,f402
  f392: extruded ~2x0.37mm, area 0.9mm2, adj f0,f1,f391,f393
  f393: extruded ~2x0.45mm, area 1mm2, adj f0,f1,f392,f394
  f394: extruded ~2x0.47mm, area 1mm2, adj f0,f1,f393,f395
  f395: extruded ~2x0.45mm, area 0.9mm2, adj f0,f1,f394,f396
  f396: plane 2x0.02mm, normal (0,-1,0), area 0mm2, adj f0,f1,f395,f397
  f397: plane 2x0.87mm, normal (-1,0,0), area 1.7mm2, adj f0,f1,f396,f398
  f398: plane 2x0.03mm, normal (0,1,0), area 0.1mm2, adj f0,f1,f397,f399
  f399: extruded ~2x0.39mm, area 0.8mm2, adj f0,f1,f398,f400
  f400: extruded ~2x0.42mm, area 0.9mm2, adj f0,f1,f399,f401
  f401: extruded ~2x0.41mm, area 0.9mm2, adj f0,f1,f400,f402
  f402: extruded ~2x0.33mm, area 0.7mm2, adj f0,f1,f391,f401
  f403: extruded ~2x0.72mm, area 1.5mm2, adj f0,f1,f404,f416
  f404: extruded ~2x0.53mm, area 1.3mm2, adj f0,f1,f403,f405
  f405: extruded ~2x0.55mm, area 1.4mm2, adj f0,f1,f404,f406
  f406: extruded ~2x0.61mm, area 1.4mm2, adj f0,f1,f405,f407
  f407: plane 2x1.05mm, normal (-1,0,0), area 2.1mm2, adj f0,f1,f406,f408
  f408: extruded ~2x0.49mm, area 1.2mm2, adj f0,f1,f407,f409
  f409: extruded ~2x0.58mm, area 1.2mm2, adj f0,f1,f408,f410
  f410: extruded ~2x0.51mm, area 1.1mm2, adj f0,f1,f409,f411
  f411: extruded ~2x0.49mm, area 1.2mm2, adj f0,f1,f410,f412
  f412: plane 2x0.96mm, normal (-1,0,0), area 1.9mm2, adj f0,f1,f411,f413
  f413: extruded ~2x0.67mm, area 1.4mm2, adj f0,f1,f412,f414
  f414: extruded ~2x0.55mm, area 1.4mm2, adj f0,f1,f413,f415
  f415: extruded ~2x0.56mm, area 1.4mm2, adj f0,f1,f414,f416
  f416: extruded ~2x0.72mm, area 1.5mm2, adj f0,f1,f403,f415
  f417: extruded ~2x0.09mm, area 0.2mm2, adj f0,f1,f418,f427
  f418: extruded ~2x0.21mm, area 0.5mm2, adj f0,f1,f417,f419
  f419: extruded ~2x0.27mm, area 0.6mm2, adj f0,f1,f418,f420
  f420: extruded ~2x0.26mm, area 0.6mm2, adj f0,f1,f419,f421
  f421: extruded ~2x0.67mm, area 1.4mm2, adj f0,f1,f420,f422
  f422: extruded ~2x0.82mm, area 1.7mm2, adj f0,f1,f421,f423
  f423: plane 2x0.93mm, normal (1,0,0), area 1.9mm2, adj f0,f1,f422,f424
  f424: extruded ~2x0.47mm, area 0.9mm2, adj f0,f1,f423,f425
  f425: extruded ~2x0.3mm, area 0.6mm2, adj f0,f1,f424,f426
  f426: extruded ~2x0.18mm, area 0.4mm2, adj f0,f1,f425,f427
  f427: extruded ~2x0.11mm, area 0.3mm2, adj f0,f1,f417,f426
PLACE A rot(axis=(1,0,0),180deg) t=(-5.23,-9.22,-77.92)mm
PLACE B rot(axis=(0,0,1),180deg) t=(-4.87,-9.22,-135.76)mm
PLACE C t=(-4.83,-9.45,-141.36)mm fixed
MATE slider B.f2 <-> C.f0  axis (0,0,-1) through (-4.87,-15.69,-156.02)mm
MATE slider A.f8 <-> B.f1  axis (0,0,-1) through (-4.87,-9.22,-83.42)mm
